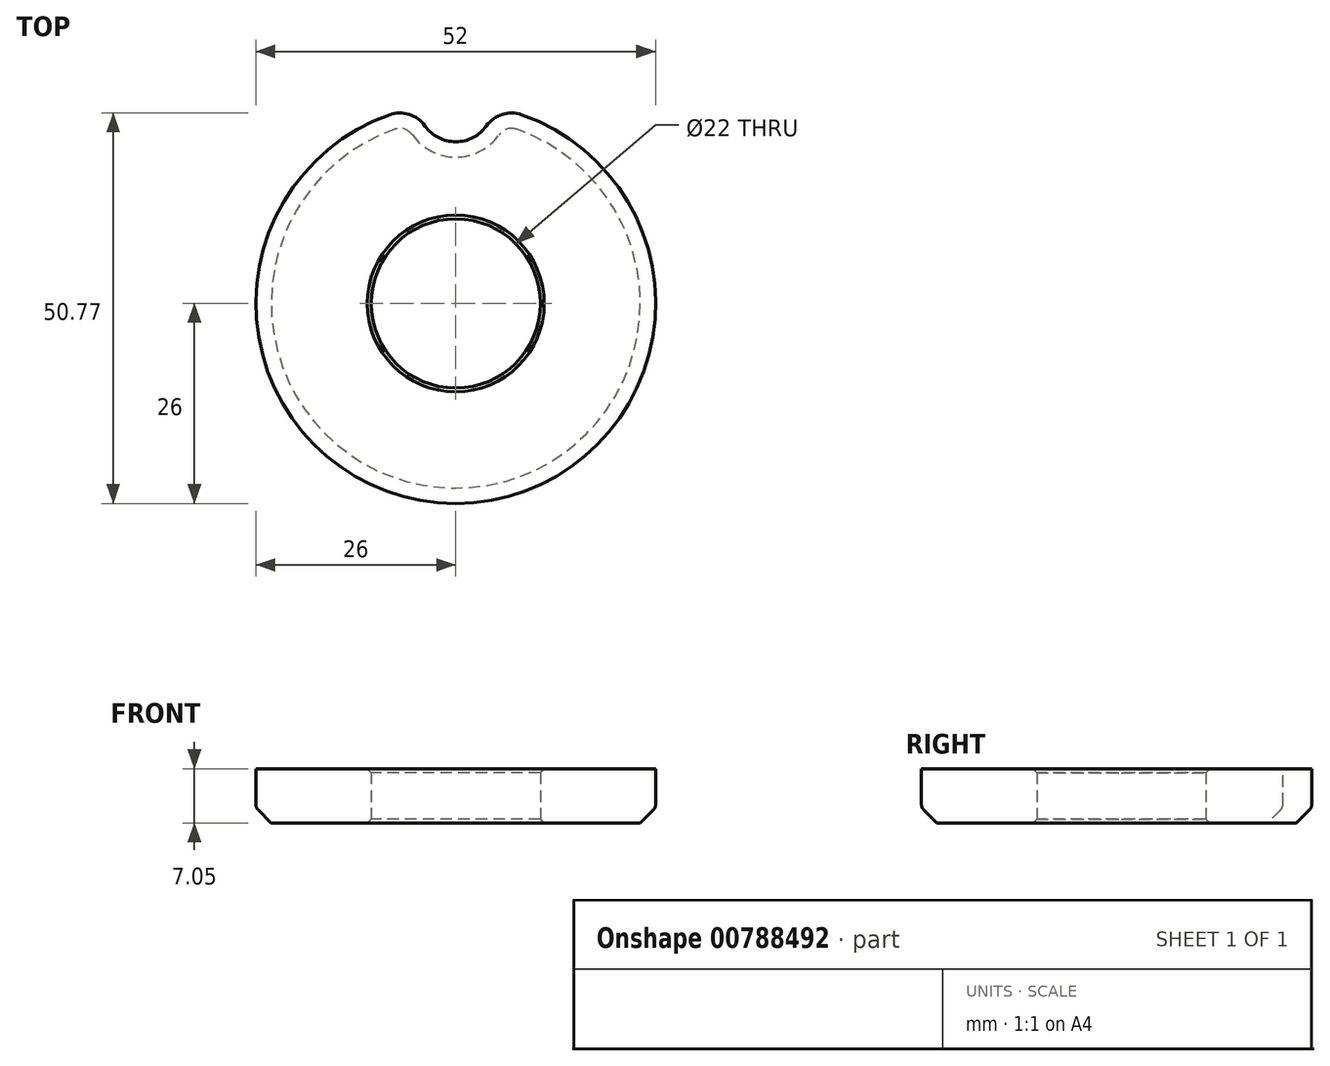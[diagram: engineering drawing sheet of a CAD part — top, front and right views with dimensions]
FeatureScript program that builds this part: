
annotation { "Feature Type Name" : "Feature", "Feature Type Description" : "" }
export const myFeature = defineFeature(function(context is Context, id is Id, definition is map)
    precondition{}
    {
        {
            var Q0;
            Q0=qCreatedBy(makeId("Top.planeOp"),FACE);
            var sketch = newSketch(context, id + "F0", { "sketchPlane" : qUnion([Q0])});
            skCircle(sketch, "E0", {"center": v(0, 0) * mm, "radius": 11 * mm});
            skCircle(sketch, "E1", {"center": v(0, 0) * mm, "radius": 26 * mm});
            skSolve(sketch);
        }
        {
            var Q0;
            Q0=makeQuery(id+"F0.imprint","IMPRINT",FACE,{"disambiguationData":[TD([[makeQuery(id+"F0.imprint","IMPRINT",EDGE,{"derivedFrom":sQuery(id+"F0.wireOp",EDGE,"E0")}),-1.0]])]});
            extrude(context, id + "F1", {"entities" : qUnion([Q0]), "depth" : 7.05 * mm, "offsetDistance" : 25 * mm});
        }
        {
            var Q0;
            Q0=makeQuery(id+"F1.opExtrude","CAP_FACE",FACE,{"disambiguationData":[OSD([sQuery(id+"F0.wireOp",EDGE,"E0"),sQuery(id+"F0.wireOp",EDGE,"E1")])],"isStart":false});
            var sketch = newSketch(context, id + "F2", { "sketchPlane" : qUnion([Q0])});
            skCircle(sketch, "E2", {"center": v(0, 26) * mm, "radius": 4.8 * mm});
            skSolve(sketch);
        }
        {
            var Q0;
            Q0=makeQuery(id+"F2.imprint","IMPRINT",FACE,{"disambiguationData":[TD([[makeQuery(id+"F2.imprint","IMPRINT",EDGE,{"derivedFrom":makeQuery(id+"F1.opExtrude","CAP_EDGE",EDGE,{"disambiguationData":[OSD([sQuery(id+"F0.wireOp",EDGE,"E0")])],"isStart":false})}),-1.0]])]});
            var sketch = newSketch(context, id + "F3", { "sketchPlane" : qUnion([Q0])});
            skCircle(sketch, "E3", {"center": v(0, 0) * mm, "radius": 25.92 * mm, "construction": true});
            skCircle(sketch, "E4", {"center": v(0, 25.92) * mm, "radius": 4.9 * mm});
            skSolve(sketch);
        }
        {
            var Q0;
            Q0 = qSketchRegion(id + "F3", true);
            extrude(context, id + "F4", {"entities" : qUnion([Q0]), "operationType" : NewBodyOperationType.REMOVE, "oppositeDirection" : true, "depth" : 25 * mm, "offsetDistance" : 25 * mm});
        }
        {
            var Q0;
            {var subQ0=sQuery(id+"F3.wireOp",EDGE,"E4");var subQ1=sQuery(id+"F0.wireOp",EDGE,"E1");var subQ4=makeQuery(id+"F4.boolean.opBoolean","COPY",FACE,{"derivedFrom":makeQuery(id+"F4.opExtrude","SWEPT_FACE",FACE,{"disambiguationData":[OSD([subQ0])]})});Q0=makeQuery(id+"FdstZYLw7MuoTlF_1.8.F4.boolean.opBoolean","INTERSECT",EDGE,{"disambiguationData":[OD(0.0)],"derivedFrom":[makeQuery(id+"FdstZYLw7MuoTlF_1.7.F4.boolean.opBoolean","SPLIT",FACE,{"disambiguationData":[TD([subQ4])],"derivedFrom":makeQuery(id+"FdstZYLw7MuoTlF_1.6.F4.boolean.opBoolean","SPLIT",FACE,{"disambiguationData":[TD([subQ4])],"derivedFrom":makeQuery(id+"FdstZYLw7MuoTlF_1.5.F4.boolean.opBoolean","SPLIT",FACE,{"disambiguationData":[TD([subQ4])],"derivedFrom":makeQuery(id+"FdstZYLw7MuoTlF_1.4.F4.boolean.opBoolean","SPLIT",FACE,{"disambiguationData":[TD([subQ4])],"derivedFrom":makeQuery(id+"FdstZYLw7MuoTlF_1.3.F4.boolean.opBoolean","SPLIT",FACE,{"disambiguationData":[TD([subQ4])],"derivedFrom":makeQuery(id+"FdstZYLw7MuoTlF_1.2.F4.boolean.opBoolean","SPLIT",FACE,{"disambiguationData":[TD([subQ4])],"derivedFrom":makeQuery(id+"FdstZYLw7MuoTlF_1.1.F4.boolean.opBoolean","SPLIT",FACE,{"disambiguationData":[OD(0.0)],"derivedFrom":makeQuery(id+"F1.opExtrude","SWEPT_FACE",FACE,{"disambiguationData":[OSD([subQ1])]})})})})})})})}),makeQuery(id+"FdstZYLw7MuoTlF_1.8.F4.opExtrude","SWEPT_FACE",FACE,{"disambiguationData":[OSD([subQ0])]})]});}
            var Q1;
            Q1=makeQuery(id+"F4.boolean.opBoolean","INTERSECT",EDGE,{"disambiguationData":[OD(0.0)],"derivedFrom":[makeQuery(id+"F1.opExtrude","SWEPT_FACE",FACE,{"disambiguationData":[OSD([sQuery(id+"F0.wireOp",EDGE,"E1")])]}),makeQuery(id+"F4.opExtrude","SWEPT_FACE",FACE,{"disambiguationData":[OSD([sQuery(id+"F3.wireOp",EDGE,"E4")])]})]});
            var Q2;
            Q2=makeQuery(id+"F4.boolean.opBoolean","INTERSECT",EDGE,{"disambiguationData":[OD(1.0)],"derivedFrom":[makeQuery(id+"F1.opExtrude","SWEPT_FACE",FACE,{"disambiguationData":[OSD([sQuery(id+"F0.wireOp",EDGE,"E1")])]}),makeQuery(id+"F4.opExtrude","SWEPT_FACE",FACE,{"disambiguationData":[OSD([sQuery(id+"F3.wireOp",EDGE,"E4")])]})]});
            var Q3;
            Q3=makeQuery(id+"FdstZYLw7MuoTlF_1.1.F4.boolean.opBoolean","INTERSECT",EDGE,{"disambiguationData":[OD(1.0)],"derivedFrom":[makeQuery(id+"F1.opExtrude","SWEPT_FACE",FACE,{"disambiguationData":[OSD([sQuery(id+"F0.wireOp",EDGE,"E1")])]}),makeQuery(id+"FdstZYLw7MuoTlF_1.1.F4.opExtrude","SWEPT_FACE",FACE,{"disambiguationData":[OSD([sQuery(id+"F3.wireOp",EDGE,"E4")])]})]});
            var Q4;
            Q4=makeQuery(id+"FdstZYLw7MuoTlF_1.1.F4.boolean.opBoolean","INTERSECT",EDGE,{"disambiguationData":[OD(0.0)],"derivedFrom":[makeQuery(id+"F1.opExtrude","SWEPT_FACE",FACE,{"disambiguationData":[OSD([sQuery(id+"F0.wireOp",EDGE,"E1")])]}),makeQuery(id+"FdstZYLw7MuoTlF_1.1.F4.opExtrude","SWEPT_FACE",FACE,{"disambiguationData":[OSD([sQuery(id+"F3.wireOp",EDGE,"E4")])]})]});
            var Q5;
            Q5=makeQuery(id+"FdstZYLw7MuoTlF_1.2.F4.boolean.opBoolean","INTERSECT",EDGE,{"disambiguationData":[OD(1.0)],"derivedFrom":[makeQuery(id+"FdstZYLw7MuoTlF_1.1.F4.boolean.opBoolean","SPLIT",FACE,{"disambiguationData":[OD(0.0)],"derivedFrom":makeQuery(id+"F1.opExtrude","SWEPT_FACE",FACE,{"disambiguationData":[OSD([sQuery(id+"F0.wireOp",EDGE,"E1")])]})}),makeQuery(id+"FdstZYLw7MuoTlF_1.2.F4.opExtrude","SWEPT_FACE",FACE,{"disambiguationData":[OSD([sQuery(id+"F3.wireOp",EDGE,"E4")])]})]});
            var Q6;
            Q6=makeQuery(id+"FdstZYLw7MuoTlF_1.2.F4.boolean.opBoolean","INTERSECT",EDGE,{"disambiguationData":[OD(0.0)],"derivedFrom":[makeQuery(id+"FdstZYLw7MuoTlF_1.1.F4.boolean.opBoolean","SPLIT",FACE,{"disambiguationData":[OD(0.0)],"derivedFrom":makeQuery(id+"F1.opExtrude","SWEPT_FACE",FACE,{"disambiguationData":[OSD([sQuery(id+"F0.wireOp",EDGE,"E1")])]})}),makeQuery(id+"FdstZYLw7MuoTlF_1.2.F4.opExtrude","SWEPT_FACE",FACE,{"disambiguationData":[OSD([sQuery(id+"F3.wireOp",EDGE,"E4")])]})]});
            var Q7;
            {var subQ0=sQuery(id+"F3.wireOp",EDGE,"E4");var subQ1=sQuery(id+"F0.wireOp",EDGE,"E1");Q7=makeQuery(id+"FdstZYLw7MuoTlF_1.3.F4.boolean.opBoolean","INTERSECT",EDGE,{"disambiguationData":[OD(1.0)],"derivedFrom":[makeQuery(id+"FdstZYLw7MuoTlF_1.2.F4.boolean.opBoolean","SPLIT",FACE,{"disambiguationData":[TD([makeQuery(id+"F4.boolean.opBoolean","COPY",FACE,{"derivedFrom":makeQuery(id+"F4.opExtrude","SWEPT_FACE",FACE,{"disambiguationData":[OSD([subQ0])]})})])],"derivedFrom":makeQuery(id+"FdstZYLw7MuoTlF_1.1.F4.boolean.opBoolean","SPLIT",FACE,{"disambiguationData":[OD(0.0)],"derivedFrom":makeQuery(id+"F1.opExtrude","SWEPT_FACE",FACE,{"disambiguationData":[OSD([subQ1])]})})}),makeQuery(id+"FdstZYLw7MuoTlF_1.3.F4.opExtrude","SWEPT_FACE",FACE,{"disambiguationData":[OSD([subQ0])]})]});}
            var Q8;
            {var subQ0=sQuery(id+"F3.wireOp",EDGE,"E4");var subQ1=sQuery(id+"F0.wireOp",EDGE,"E1");Q8=makeQuery(id+"FdstZYLw7MuoTlF_1.3.F4.boolean.opBoolean","INTERSECT",EDGE,{"disambiguationData":[OD(0.0)],"derivedFrom":[makeQuery(id+"FdstZYLw7MuoTlF_1.2.F4.boolean.opBoolean","SPLIT",FACE,{"disambiguationData":[TD([makeQuery(id+"F4.boolean.opBoolean","COPY",FACE,{"derivedFrom":makeQuery(id+"F4.opExtrude","SWEPT_FACE",FACE,{"disambiguationData":[OSD([subQ0])]})})])],"derivedFrom":makeQuery(id+"FdstZYLw7MuoTlF_1.1.F4.boolean.opBoolean","SPLIT",FACE,{"disambiguationData":[OD(0.0)],"derivedFrom":makeQuery(id+"F1.opExtrude","SWEPT_FACE",FACE,{"disambiguationData":[OSD([subQ1])]})})}),makeQuery(id+"FdstZYLw7MuoTlF_1.3.F4.opExtrude","SWEPT_FACE",FACE,{"disambiguationData":[OSD([subQ0])]})]});}
            var Q9;
            {var subQ0=sQuery(id+"F3.wireOp",EDGE,"E4");var subQ1=sQuery(id+"F0.wireOp",EDGE,"E1");var subQ4=makeQuery(id+"F4.boolean.opBoolean","COPY",FACE,{"derivedFrom":makeQuery(id+"F4.opExtrude","SWEPT_FACE",FACE,{"disambiguationData":[OSD([subQ0])]})});Q9=makeQuery(id+"FdstZYLw7MuoTlF_1.4.F4.boolean.opBoolean","INTERSECT",EDGE,{"disambiguationData":[OD(1.0)],"derivedFrom":[makeQuery(id+"FdstZYLw7MuoTlF_1.3.F4.boolean.opBoolean","SPLIT",FACE,{"disambiguationData":[TD([subQ4])],"derivedFrom":makeQuery(id+"FdstZYLw7MuoTlF_1.2.F4.boolean.opBoolean","SPLIT",FACE,{"disambiguationData":[TD([subQ4])],"derivedFrom":makeQuery(id+"FdstZYLw7MuoTlF_1.1.F4.boolean.opBoolean","SPLIT",FACE,{"disambiguationData":[OD(0.0)],"derivedFrom":makeQuery(id+"F1.opExtrude","SWEPT_FACE",FACE,{"disambiguationData":[OSD([subQ1])]})})})}),makeQuery(id+"FdstZYLw7MuoTlF_1.4.F4.opExtrude","SWEPT_FACE",FACE,{"disambiguationData":[OSD([subQ0])]})]});}
            var Q10;
            {var subQ0=sQuery(id+"F3.wireOp",EDGE,"E4");var subQ1=sQuery(id+"F0.wireOp",EDGE,"E1");var subQ4=makeQuery(id+"F4.boolean.opBoolean","COPY",FACE,{"derivedFrom":makeQuery(id+"F4.opExtrude","SWEPT_FACE",FACE,{"disambiguationData":[OSD([subQ0])]})});Q10=makeQuery(id+"FdstZYLw7MuoTlF_1.4.F4.boolean.opBoolean","INTERSECT",EDGE,{"disambiguationData":[OD(0.0)],"derivedFrom":[makeQuery(id+"FdstZYLw7MuoTlF_1.3.F4.boolean.opBoolean","SPLIT",FACE,{"disambiguationData":[TD([subQ4])],"derivedFrom":makeQuery(id+"FdstZYLw7MuoTlF_1.2.F4.boolean.opBoolean","SPLIT",FACE,{"disambiguationData":[TD([subQ4])],"derivedFrom":makeQuery(id+"FdstZYLw7MuoTlF_1.1.F4.boolean.opBoolean","SPLIT",FACE,{"disambiguationData":[OD(0.0)],"derivedFrom":makeQuery(id+"F1.opExtrude","SWEPT_FACE",FACE,{"disambiguationData":[OSD([subQ1])]})})})}),makeQuery(id+"FdstZYLw7MuoTlF_1.4.F4.opExtrude","SWEPT_FACE",FACE,{"disambiguationData":[OSD([subQ0])]})]});}
            var Q11;
            {var subQ0=sQuery(id+"F3.wireOp",EDGE,"E4");var subQ1=sQuery(id+"F0.wireOp",EDGE,"E1");var subQ4=makeQuery(id+"F4.boolean.opBoolean","COPY",FACE,{"derivedFrom":makeQuery(id+"F4.opExtrude","SWEPT_FACE",FACE,{"disambiguationData":[OSD([subQ0])]})});Q11=makeQuery(id+"FdstZYLw7MuoTlF_1.5.F4.boolean.opBoolean","INTERSECT",EDGE,{"disambiguationData":[OD(1.0)],"derivedFrom":[makeQuery(id+"FdstZYLw7MuoTlF_1.4.F4.boolean.opBoolean","SPLIT",FACE,{"disambiguationData":[TD([subQ4])],"derivedFrom":makeQuery(id+"FdstZYLw7MuoTlF_1.3.F4.boolean.opBoolean","SPLIT",FACE,{"disambiguationData":[TD([subQ4])],"derivedFrom":makeQuery(id+"FdstZYLw7MuoTlF_1.2.F4.boolean.opBoolean","SPLIT",FACE,{"disambiguationData":[TD([subQ4])],"derivedFrom":makeQuery(id+"FdstZYLw7MuoTlF_1.1.F4.boolean.opBoolean","SPLIT",FACE,{"disambiguationData":[OD(0.0)],"derivedFrom":makeQuery(id+"F1.opExtrude","SWEPT_FACE",FACE,{"disambiguationData":[OSD([subQ1])]})})})})}),makeQuery(id+"FdstZYLw7MuoTlF_1.5.F4.opExtrude","SWEPT_FACE",FACE,{"disambiguationData":[OSD([subQ0])]})]});}
            var Q12;
            {var subQ0=sQuery(id+"F3.wireOp",EDGE,"E4");var subQ1=sQuery(id+"F0.wireOp",EDGE,"E1");var subQ4=makeQuery(id+"F4.boolean.opBoolean","COPY",FACE,{"derivedFrom":makeQuery(id+"F4.opExtrude","SWEPT_FACE",FACE,{"disambiguationData":[OSD([subQ0])]})});Q12=makeQuery(id+"FdstZYLw7MuoTlF_1.5.F4.boolean.opBoolean","INTERSECT",EDGE,{"disambiguationData":[OD(0.0)],"derivedFrom":[makeQuery(id+"FdstZYLw7MuoTlF_1.4.F4.boolean.opBoolean","SPLIT",FACE,{"disambiguationData":[TD([subQ4])],"derivedFrom":makeQuery(id+"FdstZYLw7MuoTlF_1.3.F4.boolean.opBoolean","SPLIT",FACE,{"disambiguationData":[TD([subQ4])],"derivedFrom":makeQuery(id+"FdstZYLw7MuoTlF_1.2.F4.boolean.opBoolean","SPLIT",FACE,{"disambiguationData":[TD([subQ4])],"derivedFrom":makeQuery(id+"FdstZYLw7MuoTlF_1.1.F4.boolean.opBoolean","SPLIT",FACE,{"disambiguationData":[OD(0.0)],"derivedFrom":makeQuery(id+"F1.opExtrude","SWEPT_FACE",FACE,{"disambiguationData":[OSD([subQ1])]})})})})}),makeQuery(id+"FdstZYLw7MuoTlF_1.5.F4.opExtrude","SWEPT_FACE",FACE,{"disambiguationData":[OSD([subQ0])]})]});}
            var Q13;
            {var subQ0=sQuery(id+"F3.wireOp",EDGE,"E4");var subQ1=sQuery(id+"F0.wireOp",EDGE,"E1");var subQ4=makeQuery(id+"F4.boolean.opBoolean","COPY",FACE,{"derivedFrom":makeQuery(id+"F4.opExtrude","SWEPT_FACE",FACE,{"disambiguationData":[OSD([subQ0])]})});Q13=makeQuery(id+"FdstZYLw7MuoTlF_1.6.F4.boolean.opBoolean","INTERSECT",EDGE,{"disambiguationData":[OD(1.0)],"derivedFrom":[makeQuery(id+"FdstZYLw7MuoTlF_1.5.F4.boolean.opBoolean","SPLIT",FACE,{"disambiguationData":[TD([subQ4])],"derivedFrom":makeQuery(id+"FdstZYLw7MuoTlF_1.4.F4.boolean.opBoolean","SPLIT",FACE,{"disambiguationData":[TD([subQ4])],"derivedFrom":makeQuery(id+"FdstZYLw7MuoTlF_1.3.F4.boolean.opBoolean","SPLIT",FACE,{"disambiguationData":[TD([subQ4])],"derivedFrom":makeQuery(id+"FdstZYLw7MuoTlF_1.2.F4.boolean.opBoolean","SPLIT",FACE,{"disambiguationData":[TD([subQ4])],"derivedFrom":makeQuery(id+"FdstZYLw7MuoTlF_1.1.F4.boolean.opBoolean","SPLIT",FACE,{"disambiguationData":[OD(0.0)],"derivedFrom":makeQuery(id+"F1.opExtrude","SWEPT_FACE",FACE,{"disambiguationData":[OSD([subQ1])]})})})})})}),makeQuery(id+"FdstZYLw7MuoTlF_1.6.F4.opExtrude","SWEPT_FACE",FACE,{"disambiguationData":[OSD([subQ0])]})]});}
            var Q14;
            {var subQ0=sQuery(id+"F3.wireOp",EDGE,"E4");var subQ1=sQuery(id+"F0.wireOp",EDGE,"E1");var subQ4=makeQuery(id+"F4.boolean.opBoolean","COPY",FACE,{"derivedFrom":makeQuery(id+"F4.opExtrude","SWEPT_FACE",FACE,{"disambiguationData":[OSD([subQ0])]})});Q14=makeQuery(id+"FdstZYLw7MuoTlF_1.6.F4.boolean.opBoolean","INTERSECT",EDGE,{"disambiguationData":[OD(0.0)],"derivedFrom":[makeQuery(id+"FdstZYLw7MuoTlF_1.5.F4.boolean.opBoolean","SPLIT",FACE,{"disambiguationData":[TD([subQ4])],"derivedFrom":makeQuery(id+"FdstZYLw7MuoTlF_1.4.F4.boolean.opBoolean","SPLIT",FACE,{"disambiguationData":[TD([subQ4])],"derivedFrom":makeQuery(id+"FdstZYLw7MuoTlF_1.3.F4.boolean.opBoolean","SPLIT",FACE,{"disambiguationData":[TD([subQ4])],"derivedFrom":makeQuery(id+"FdstZYLw7MuoTlF_1.2.F4.boolean.opBoolean","SPLIT",FACE,{"disambiguationData":[TD([subQ4])],"derivedFrom":makeQuery(id+"FdstZYLw7MuoTlF_1.1.F4.boolean.opBoolean","SPLIT",FACE,{"disambiguationData":[OD(0.0)],"derivedFrom":makeQuery(id+"F1.opExtrude","SWEPT_FACE",FACE,{"disambiguationData":[OSD([subQ1])]})})})})})}),makeQuery(id+"FdstZYLw7MuoTlF_1.6.F4.opExtrude","SWEPT_FACE",FACE,{"disambiguationData":[OSD([subQ0])]})]});}
            var Q15;
            {var subQ0=sQuery(id+"F3.wireOp",EDGE,"E4");var subQ1=sQuery(id+"F0.wireOp",EDGE,"E1");var subQ4=makeQuery(id+"F4.boolean.opBoolean","COPY",FACE,{"derivedFrom":makeQuery(id+"F4.opExtrude","SWEPT_FACE",FACE,{"disambiguationData":[OSD([subQ0])]})});Q15=makeQuery(id+"FdstZYLw7MuoTlF_1.7.F4.boolean.opBoolean","INTERSECT",EDGE,{"disambiguationData":[OD(1.0)],"derivedFrom":[makeQuery(id+"FdstZYLw7MuoTlF_1.6.F4.boolean.opBoolean","SPLIT",FACE,{"disambiguationData":[TD([subQ4])],"derivedFrom":makeQuery(id+"FdstZYLw7MuoTlF_1.5.F4.boolean.opBoolean","SPLIT",FACE,{"disambiguationData":[TD([subQ4])],"derivedFrom":makeQuery(id+"FdstZYLw7MuoTlF_1.4.F4.boolean.opBoolean","SPLIT",FACE,{"disambiguationData":[TD([subQ4])],"derivedFrom":makeQuery(id+"FdstZYLw7MuoTlF_1.3.F4.boolean.opBoolean","SPLIT",FACE,{"disambiguationData":[TD([subQ4])],"derivedFrom":makeQuery(id+"FdstZYLw7MuoTlF_1.2.F4.boolean.opBoolean","SPLIT",FACE,{"disambiguationData":[TD([subQ4])],"derivedFrom":makeQuery(id+"FdstZYLw7MuoTlF_1.1.F4.boolean.opBoolean","SPLIT",FACE,{"disambiguationData":[OD(0.0)],"derivedFrom":makeQuery(id+"F1.opExtrude","SWEPT_FACE",FACE,{"disambiguationData":[OSD([subQ1])]})})})})})})}),makeQuery(id+"FdstZYLw7MuoTlF_1.7.F4.opExtrude","SWEPT_FACE",FACE,{"disambiguationData":[OSD([subQ0])]})]});}
            var Q16;
            {var subQ0=sQuery(id+"F3.wireOp",EDGE,"E4");var subQ1=sQuery(id+"F0.wireOp",EDGE,"E1");var subQ4=makeQuery(id+"F4.boolean.opBoolean","COPY",FACE,{"derivedFrom":makeQuery(id+"F4.opExtrude","SWEPT_FACE",FACE,{"disambiguationData":[OSD([subQ0])]})});Q16=makeQuery(id+"FdstZYLw7MuoTlF_1.7.F4.boolean.opBoolean","INTERSECT",EDGE,{"disambiguationData":[OD(0.0)],"derivedFrom":[makeQuery(id+"FdstZYLw7MuoTlF_1.6.F4.boolean.opBoolean","SPLIT",FACE,{"disambiguationData":[TD([subQ4])],"derivedFrom":makeQuery(id+"FdstZYLw7MuoTlF_1.5.F4.boolean.opBoolean","SPLIT",FACE,{"disambiguationData":[TD([subQ4])],"derivedFrom":makeQuery(id+"FdstZYLw7MuoTlF_1.4.F4.boolean.opBoolean","SPLIT",FACE,{"disambiguationData":[TD([subQ4])],"derivedFrom":makeQuery(id+"FdstZYLw7MuoTlF_1.3.F4.boolean.opBoolean","SPLIT",FACE,{"disambiguationData":[TD([subQ4])],"derivedFrom":makeQuery(id+"FdstZYLw7MuoTlF_1.2.F4.boolean.opBoolean","SPLIT",FACE,{"disambiguationData":[TD([subQ4])],"derivedFrom":makeQuery(id+"FdstZYLw7MuoTlF_1.1.F4.boolean.opBoolean","SPLIT",FACE,{"disambiguationData":[OD(0.0)],"derivedFrom":makeQuery(id+"F1.opExtrude","SWEPT_FACE",FACE,{"disambiguationData":[OSD([subQ1])]})})})})})})}),makeQuery(id+"FdstZYLw7MuoTlF_1.7.F4.opExtrude","SWEPT_FACE",FACE,{"disambiguationData":[OSD([subQ0])]})]});}
            var Q17;
            {var subQ0=sQuery(id+"F3.wireOp",EDGE,"E4");var subQ1=sQuery(id+"F0.wireOp",EDGE,"E1");var subQ4=makeQuery(id+"F4.boolean.opBoolean","COPY",FACE,{"derivedFrom":makeQuery(id+"F4.opExtrude","SWEPT_FACE",FACE,{"disambiguationData":[OSD([subQ0])]})});Q17=makeQuery(id+"FdstZYLw7MuoTlF_1.8.F4.boolean.opBoolean","INTERSECT",EDGE,{"disambiguationData":[OD(1.0)],"derivedFrom":[makeQuery(id+"FdstZYLw7MuoTlF_1.7.F4.boolean.opBoolean","SPLIT",FACE,{"disambiguationData":[TD([subQ4])],"derivedFrom":makeQuery(id+"FdstZYLw7MuoTlF_1.6.F4.boolean.opBoolean","SPLIT",FACE,{"disambiguationData":[TD([subQ4])],"derivedFrom":makeQuery(id+"FdstZYLw7MuoTlF_1.5.F4.boolean.opBoolean","SPLIT",FACE,{"disambiguationData":[TD([subQ4])],"derivedFrom":makeQuery(id+"FdstZYLw7MuoTlF_1.4.F4.boolean.opBoolean","SPLIT",FACE,{"disambiguationData":[TD([subQ4])],"derivedFrom":makeQuery(id+"FdstZYLw7MuoTlF_1.3.F4.boolean.opBoolean","SPLIT",FACE,{"disambiguationData":[TD([subQ4])],"derivedFrom":makeQuery(id+"FdstZYLw7MuoTlF_1.2.F4.boolean.opBoolean","SPLIT",FACE,{"disambiguationData":[TD([subQ4])],"derivedFrom":makeQuery(id+"FdstZYLw7MuoTlF_1.1.F4.boolean.opBoolean","SPLIT",FACE,{"disambiguationData":[OD(0.0)],"derivedFrom":makeQuery(id+"F1.opExtrude","SWEPT_FACE",FACE,{"disambiguationData":[OSD([subQ1])]})})})})})})})}),makeQuery(id+"FdstZYLw7MuoTlF_1.8.F4.opExtrude","SWEPT_FACE",FACE,{"disambiguationData":[OSD([subQ0])]})]});}
            fillet(context, id + "F5", {"entities" : qUnion([Q0, Q1, Q2, Q3, Q4, Q5, Q6, Q7, Q8, Q9, Q10, Q11, Q12, Q13, Q14, Q15, Q16, Q17]), "radius" : 4 * mm, "tangentPropagation" : true, "allowEdgeOverflow" : false});
        }
        {
            var Q0;
            Q0=makeQuery(id+"F1.opExtrude","CAP_EDGE",EDGE,{"disambiguationData":[OSD([sQuery(id+"F0.wireOp",EDGE,"E0")])],"isStart":true});
            var Q1;
            Q1=makeQuery(id+"F1.opExtrude","CAP_EDGE",EDGE,{"disambiguationData":[OSD([sQuery(id+"F0.wireOp",EDGE,"E0")])],"isStart":false});
            chamfer(context, id + "F6", {"entities" : qUnion([Q0, Q1]), "width" : 0.5 * mm, "tangentPropagation" : true});
        }
        {
            var Q0;
            Q0=makeQuery(id+"FdstZYLw7MuoTlF_1.5.F4.boolean.opBoolean","INTERSECT",EDGE,{"derivedFrom":[makeQuery(id+"F1.opExtrude","CAP_FACE",FACE,{"disambiguationData":[OSD([sQuery(id+"F0.wireOp",EDGE,"E0"),sQuery(id+"F0.wireOp",EDGE,"E1")])],"isStart":true}),makeQuery(id+"FdstZYLw7MuoTlF_1.5.F4.opExtrude","SWEPT_FACE",FACE,{"disambiguationData":[OSD([sQuery(id+"F3.wireOp",EDGE,"E4")])]})]});
            var Q1;
            Q1=makeQuery(id+"FdstZYLw7MuoTlF_1.6.F4.boolean.opBoolean","INTERSECT",EDGE,{"derivedFrom":[makeQuery(id+"F1.opExtrude","CAP_FACE",FACE,{"disambiguationData":[OSD([sQuery(id+"F0.wireOp",EDGE,"E0"),sQuery(id+"F0.wireOp",EDGE,"E1")])],"isStart":true}),makeQuery(id+"FdstZYLw7MuoTlF_1.6.F4.opExtrude","SWEPT_FACE",FACE,{"disambiguationData":[OSD([sQuery(id+"F3.wireOp",EDGE,"E4")])]})]});
            var Q2;
            {var subQ0=sQuery(id+"F0.wireOp",EDGE,"E1");Q2=makeQuery(id+"F5.opFillet","BLEND_EDGE",EDGE,{"blendedFrom":[makeQuery(id+"FdstZYLw7MuoTlF_1.1.F4.boolean.opBoolean","INTERSECT",EDGE,{"disambiguationData":[OD(1.0)],"derivedFrom":[makeQuery(id+"F1.opExtrude","SWEPT_FACE",FACE,{"disambiguationData":[OSD([subQ0])]}),makeQuery(id+"FdstZYLw7MuoTlF_1.1.F4.opExtrude","SWEPT_FACE",FACE,{"disambiguationData":[OSD([sQuery(id+"F3.wireOp",EDGE,"E4")])]})]}),makeQuery(id+"F1.opExtrude","CAP_FACE",FACE,{"disambiguationData":[OSD([sQuery(id+"F0.wireOp",EDGE,"E0"),subQ0])],"isStart":true})],"blendedInto":[makeQuery(id+"F1.opExtrude","CAP_FACE",FACE,{"disambiguationData":[OSD([sQuery(id+"F0.wireOp",EDGE,"E0"),subQ0])],"isStart":true})]});}
            var Q3;
            {var subQ0=sQuery(id+"F0.wireOp",EDGE,"E1");Q3=makeQuery(id+"F5.opFillet","BLEND_EDGE",EDGE,{"blendedFrom":[makeQuery(id+"F4.boolean.opBoolean","INTERSECT",EDGE,{"disambiguationData":[OD(1.0)],"derivedFrom":[makeQuery(id+"F1.opExtrude","SWEPT_FACE",FACE,{"disambiguationData":[OSD([subQ0])]}),makeQuery(id+"F4.opExtrude","SWEPT_FACE",FACE,{"disambiguationData":[OSD([sQuery(id+"F3.wireOp",EDGE,"E4")])]})]}),makeQuery(id+"F1.opExtrude","CAP_FACE",FACE,{"disambiguationData":[OSD([sQuery(id+"F0.wireOp",EDGE,"E0"),subQ0])],"isStart":true})],"blendedInto":[makeQuery(id+"F1.opExtrude","CAP_FACE",FACE,{"disambiguationData":[OSD([sQuery(id+"F0.wireOp",EDGE,"E0"),subQ0])],"isStart":true})]});}
            var Q4;
            {var subQ0=sQuery(id+"F0.wireOp",EDGE,"E1");var subQ1=sQuery(id+"F0.wireOp",EDGE,"E0");var subQ2=makeQuery(id+"F1.opExtrude","CAP_FACE",FACE,{"disambiguationData":[OSD([subQ1,subQ0])],"isStart":true});var subQ3=sQuery(id+"F3.wireOp",EDGE,"E4");Q4=makeQuery(id+"F5.opFillet","BLEND_EDGE",EDGE,{"blendedFrom":[makeQuery(id+"FdstZYLw7MuoTlF_1.3.F4.boolean.opBoolean","INTERSECT",EDGE,{"disambiguationData":[OD(1.0)],"derivedFrom":[makeQuery(id+"FdstZYLw7MuoTlF_1.2.F4.boolean.opBoolean","SPLIT",FACE,{"disambiguationData":[TD([makeQuery(id+"F4.boolean.opBoolean","COPY",FACE,{"derivedFrom":makeQuery(id+"F4.opExtrude","SWEPT_FACE",FACE,{"disambiguationData":[OSD([subQ3])]})})])],"derivedFrom":makeQuery(id+"FdstZYLw7MuoTlF_1.1.F4.boolean.opBoolean","SPLIT",FACE,{"disambiguationData":[OD(0.0)],"derivedFrom":makeQuery(id+"F1.opExtrude","SWEPT_FACE",FACE,{"disambiguationData":[OSD([subQ0])]})})}),makeQuery(id+"FdstZYLw7MuoTlF_1.3.F4.opExtrude","SWEPT_FACE",FACE,{"disambiguationData":[OSD([subQ3])]})]}),subQ2],"blendedInto":[subQ2]});}
            var Q5;
            {var subQ0=sQuery(id+"F0.wireOp",EDGE,"E1");Q5=makeQuery(id+"F5.opFillet","BLEND_EDGE",EDGE,{"blendedFrom":[makeQuery(id+"FdstZYLw7MuoTlF_1.2.F4.boolean.opBoolean","INTERSECT",EDGE,{"disambiguationData":[OD(0.0)],"derivedFrom":[makeQuery(id+"FdstZYLw7MuoTlF_1.1.F4.boolean.opBoolean","SPLIT",FACE,{"disambiguationData":[OD(0.0)],"derivedFrom":makeQuery(id+"F1.opExtrude","SWEPT_FACE",FACE,{"disambiguationData":[OSD([subQ0])]})}),makeQuery(id+"FdstZYLw7MuoTlF_1.2.F4.opExtrude","SWEPT_FACE",FACE,{"disambiguationData":[OSD([sQuery(id+"F3.wireOp",EDGE,"E4")])]})]}),makeQuery(id+"F1.opExtrude","CAP_FACE",FACE,{"disambiguationData":[OSD([sQuery(id+"F0.wireOp",EDGE,"E0"),subQ0])],"isStart":true})],"blendedInto":[makeQuery(id+"F1.opExtrude","CAP_FACE",FACE,{"disambiguationData":[OSD([sQuery(id+"F0.wireOp",EDGE,"E0"),subQ0])],"isStart":true})]});}
            var Q6;
            {var subQ0=sQuery(id+"F0.wireOp",EDGE,"E1");var subQ1=sQuery(id+"F0.wireOp",EDGE,"E0");var subQ2=makeQuery(id+"F1.opExtrude","CAP_FACE",FACE,{"disambiguationData":[OSD([subQ1,subQ0])],"isStart":true});var subQ3=sQuery(id+"F3.wireOp",EDGE,"E4");var subQ4=makeQuery(id+"F4.boolean.opBoolean","COPY",FACE,{"derivedFrom":makeQuery(id+"F4.opExtrude","SWEPT_FACE",FACE,{"disambiguationData":[OSD([subQ3])]})});Q6=makeQuery(id+"F5.opFillet","BLEND_EDGE",EDGE,{"blendedFrom":[makeQuery(id+"FdstZYLw7MuoTlF_1.8.F4.boolean.opBoolean","INTERSECT",EDGE,{"disambiguationData":[OD(1.0)],"derivedFrom":[makeQuery(id+"FdstZYLw7MuoTlF_1.7.F4.boolean.opBoolean","SPLIT",FACE,{"disambiguationData":[TD([subQ4])],"derivedFrom":makeQuery(id+"FdstZYLw7MuoTlF_1.6.F4.boolean.opBoolean","SPLIT",FACE,{"disambiguationData":[TD([subQ4])],"derivedFrom":makeQuery(id+"FdstZYLw7MuoTlF_1.5.F4.boolean.opBoolean","SPLIT",FACE,{"disambiguationData":[TD([subQ4])],"derivedFrom":makeQuery(id+"FdstZYLw7MuoTlF_1.4.F4.boolean.opBoolean","SPLIT",FACE,{"disambiguationData":[TD([subQ4])],"derivedFrom":makeQuery(id+"FdstZYLw7MuoTlF_1.3.F4.boolean.opBoolean","SPLIT",FACE,{"disambiguationData":[TD([subQ4])],"derivedFrom":makeQuery(id+"FdstZYLw7MuoTlF_1.2.F4.boolean.opBoolean","SPLIT",FACE,{"disambiguationData":[TD([subQ4])],"derivedFrom":makeQuery(id+"FdstZYLw7MuoTlF_1.1.F4.boolean.opBoolean","SPLIT",FACE,{"disambiguationData":[OD(0.0)],"derivedFrom":makeQuery(id+"F1.opExtrude","SWEPT_FACE",FACE,{"disambiguationData":[OSD([subQ0])]})})})})})})})}),makeQuery(id+"FdstZYLw7MuoTlF_1.8.F4.opExtrude","SWEPT_FACE",FACE,{"disambiguationData":[OSD([subQ3])]})]}),subQ2],"blendedInto":[subQ2]});}
            var Q7;
            {var subQ0=sQuery(id+"F0.wireOp",EDGE,"E1");var subQ1=sQuery(id+"F0.wireOp",EDGE,"E0");var subQ2=makeQuery(id+"F1.opExtrude","CAP_FACE",FACE,{"disambiguationData":[OSD([subQ1,subQ0])],"isStart":true});var subQ3=sQuery(id+"F3.wireOp",EDGE,"E4");var subQ4=makeQuery(id+"F4.boolean.opBoolean","COPY",FACE,{"derivedFrom":makeQuery(id+"F4.opExtrude","SWEPT_FACE",FACE,{"disambiguationData":[OSD([subQ3])]})});Q7=makeQuery(id+"F5.opFillet","BLEND_EDGE",EDGE,{"blendedFrom":[makeQuery(id+"FdstZYLw7MuoTlF_1.7.F4.boolean.opBoolean","INTERSECT",EDGE,{"disambiguationData":[OD(0.0)],"derivedFrom":[makeQuery(id+"FdstZYLw7MuoTlF_1.6.F4.boolean.opBoolean","SPLIT",FACE,{"disambiguationData":[TD([subQ4])],"derivedFrom":makeQuery(id+"FdstZYLw7MuoTlF_1.5.F4.boolean.opBoolean","SPLIT",FACE,{"disambiguationData":[TD([subQ4])],"derivedFrom":makeQuery(id+"FdstZYLw7MuoTlF_1.4.F4.boolean.opBoolean","SPLIT",FACE,{"disambiguationData":[TD([subQ4])],"derivedFrom":makeQuery(id+"FdstZYLw7MuoTlF_1.3.F4.boolean.opBoolean","SPLIT",FACE,{"disambiguationData":[TD([subQ4])],"derivedFrom":makeQuery(id+"FdstZYLw7MuoTlF_1.2.F4.boolean.opBoolean","SPLIT",FACE,{"disambiguationData":[TD([subQ4])],"derivedFrom":makeQuery(id+"FdstZYLw7MuoTlF_1.1.F4.boolean.opBoolean","SPLIT",FACE,{"disambiguationData":[OD(0.0)],"derivedFrom":makeQuery(id+"F1.opExtrude","SWEPT_FACE",FACE,{"disambiguationData":[OSD([subQ0])]})})})})})})}),makeQuery(id+"FdstZYLw7MuoTlF_1.7.F4.opExtrude","SWEPT_FACE",FACE,{"disambiguationData":[OSD([subQ3])]})]}),subQ2],"blendedInto":[subQ2]});}
            var Q8;
            Q8=makeQuery(id+"FdstZYLw7MuoTlF_1.1.F4.boolean.opBoolean","COPY",EDGE,{"derivedFrom":makeQuery(id+"FdstZYLw7MuoTlF_1.1.F4.opExtrude","CAP_EDGE",EDGE,{"disambiguationData":[OSD([sQuery(id+"F3.wireOp",EDGE,"E4")])],"isStart":true})});
            chamfer(context, id + "F7", {"entities" : qUnion([Q0, Q1, Q2, Q3, Q4, Q5, Q6, Q7, Q8]), "width" : 2 * mm, "tangentPropagation" : true});
        }
        {
            var Q0;
            {var subQ0=sQuery(id+"F3.wireOp",EDGE,"E4");var subQ1=sQuery(id+"F0.wireOp",EDGE,"E1");var subQ2=makeQuery(id+"F4.boolean.opBoolean","INTERSECT",EDGE,{"disambiguationData":[OD(0.0)],"derivedFrom":[makeQuery(id+"F1.opExtrude","SWEPT_FACE",FACE,{"disambiguationData":[OSD([subQ1])]}),makeQuery(id+"F4.opExtrude","SWEPT_FACE",FACE,{"disambiguationData":[OSD([subQ0])]})]});Q0=makeQuery(id+"F7.opChamfer","BLEND_EDGE",EDGE,{"blendedFrom":[makeQuery(id+"F5.opFillet","BLEND_EDGE",EDGE,{"blendedFrom":[subQ2,makeQuery(id+"F1.opExtrude","CAP_FACE",FACE,{"disambiguationData":[OSD([sQuery(id+"F0.wireOp",EDGE,"E0"),subQ1])],"isStart":false})],"blendedInto":[makeQuery(id+"F1.opExtrude","CAP_FACE",FACE,{"disambiguationData":[OSD([sQuery(id+"F0.wireOp",EDGE,"E0"),subQ1])],"isStart":false})]}),makeQuery(id+"F5.opFillet","BLEND_FACE",FACE,{"disambiguationData":[OSD([subQ1,subQ0]),TDD([subQ2])]})],"blendedInto":[makeQuery(id+"F5.opFillet","BLEND_FACE",FACE,{"disambiguationData":[OSD([subQ1,subQ0]),TDD([subQ2])]})]});}
            var Q1;
            {var subQ0=sQuery(id+"F3.wireOp",EDGE,"E4");var subQ1=sQuery(id+"F0.wireOp",EDGE,"E1");var subQ2=makeQuery(id+"F4.boolean.opBoolean","INTERSECT",EDGE,{"disambiguationData":[OD(0.0)],"derivedFrom":[makeQuery(id+"F1.opExtrude","SWEPT_FACE",FACE,{"disambiguationData":[OSD([subQ1])]}),makeQuery(id+"F4.opExtrude","SWEPT_FACE",FACE,{"disambiguationData":[OSD([subQ0])]})]});Q1=makeQuery(id+"F7.opChamfer","BLEND_EDGE",EDGE,{"blendedFrom":[makeQuery(id+"F5.opFillet","BLEND_EDGE",EDGE,{"blendedFrom":[subQ2,makeQuery(id+"F1.opExtrude","CAP_FACE",FACE,{"disambiguationData":[OSD([sQuery(id+"F0.wireOp",EDGE,"E0"),subQ1])],"isStart":true})],"blendedInto":[makeQuery(id+"F1.opExtrude","CAP_FACE",FACE,{"disambiguationData":[OSD([sQuery(id+"F0.wireOp",EDGE,"E0"),subQ1])],"isStart":true})]}),makeQuery(id+"F5.opFillet","BLEND_FACE",FACE,{"disambiguationData":[OSD([subQ1,subQ0]),TDD([subQ2])]})],"blendedInto":[makeQuery(id+"F5.opFillet","BLEND_FACE",FACE,{"disambiguationData":[OSD([subQ1,subQ0]),TDD([subQ2])]})]});}
            fillet(context, id + "F8", {"entities" : qUnion([Q0, Q1]), "radius" : 1 * mm, "tangentPropagation" : true, "allowEdgeOverflow" : false});
        }
    });
